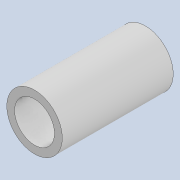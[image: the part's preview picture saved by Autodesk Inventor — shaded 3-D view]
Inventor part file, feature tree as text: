
AUTODESK INVENTOR PART (.ipt)
format: ipt  version: 2020 (Build 240168000, 168)  size: 110,592 bytes
history: native  units: mm
features: extrude x1, sketch x1
ambient origin geometry x8: Origin, YZ Plane, XZ Plane, XY Plane, X Axis, Y Axis, Z Axis, Center Point
bodies: Solid1 (feature_tree)
feature tree (2):
  extrude  "Extrusion1"  Depth=30.0mm
  sketch  "Sketch1"  dims[d0=15.0mm d1=10.8mm d2=30.0mm d3=0.0mm]
